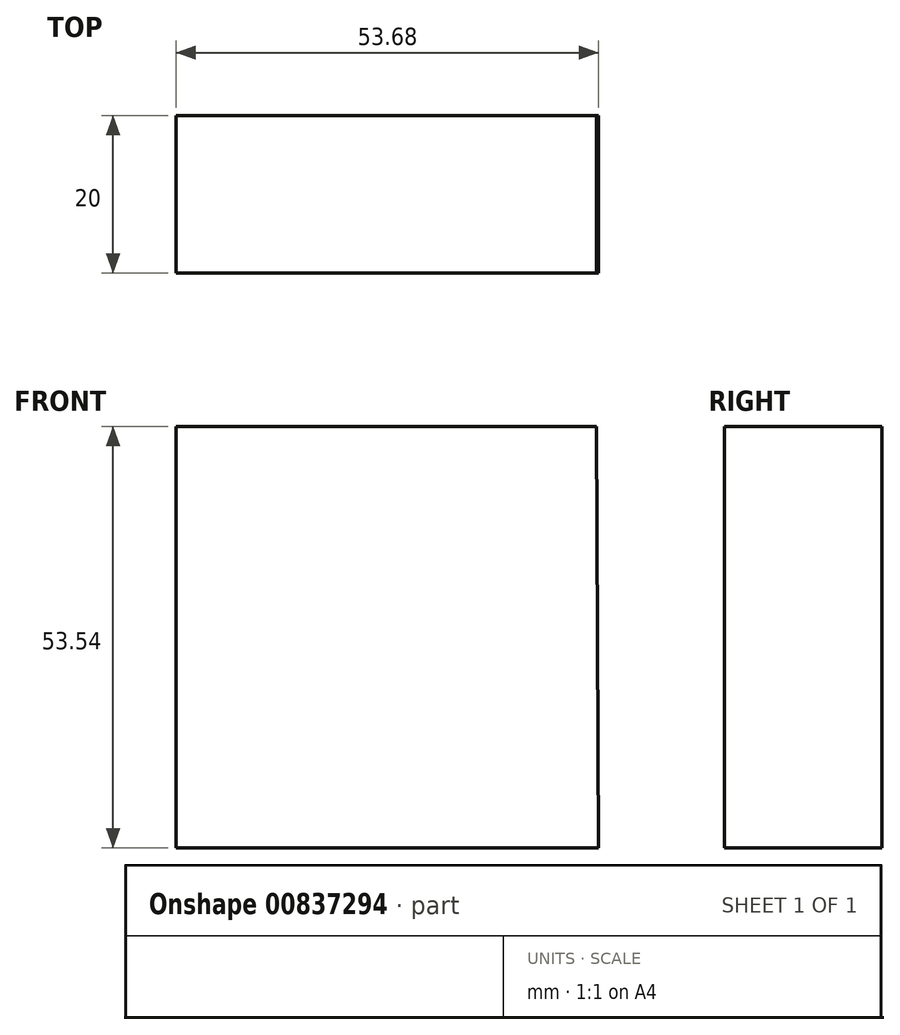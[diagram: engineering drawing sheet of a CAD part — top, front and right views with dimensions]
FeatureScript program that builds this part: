
annotation { "Feature Type Name" : "Feature", "Feature Type Description" : "" }
export const myFeature = defineFeature(function(context is Context, id is Id, definition is map)
    precondition{}
    {
        {
            var Q0;
            Q0=qCreatedBy(makeId("Front.planeOp"),FACE);
            var sketch = newSketch(context, id + "F0", { "sketchPlane" : qUnion([Q0])});
            skLineSegment(sketch, "E0", {"start": v(0, 27.9) * mm, "end": v(0, -25.64) * mm});
            skLineSegment(sketch, "E1", {"start": v(0, 27.9) * mm, "end": v(53.4, 27.9) * mm});
            skLineSegment(sketch, "E2", {"start": v(0, -25.64) * mm, "end": v(53.68, -25.64) * mm});
            skLineSegment(sketch, "E3", {"start": v(53.68, -25.64) * mm, "end": v(53.4, 27.9) * mm});
            skLineSegment(sketch, "E4", {"start": v(6.1, 20.82) * mm, "end": v(6.1, -21.1) * mm});
            skLineSegment(sketch, "E5", {"start": v(6.1, -21.1) * mm, "end": v(46.6, -21.1) * mm});
            skLineSegment(sketch, "E6", {"start": v(6.1, 20.82) * mm, "end": v(46.6, 20.82) * mm});
            skLineSegment(sketch, "E7", {"start": v(46.6, 20.82) * mm, "end": v(46.6, -18.84) * mm});
            skSolve(sketch);
        }
        {
            var Q0;
            Q0=makeQuery(id+"F0.imprint","IMPRINT",FACE,{"disambiguationData":[TD([[makeQuery(id+"F0.imprint","IMPRINT",EDGE,{"derivedFrom":sQuery(id+"F0.wireOp",EDGE,"E0")}),1.0]])]});
            extrude(context, id + "F1", {"entities" : qUnion([Q0]), "depth" : 20 * mm, "offsetDistance" : 25 * mm});
        }
        {
            var Q0;
            Q0 = qSketchRegion(id + "F0", true);
            var Q1;
            Q1=makeQuery(id+"F1.opExtrude","CAP_FACE",FACE,{"disambiguationData":[OSD([sQuery(id+"F0.wireOp",EDGE,"E0"),sQuery(id+"F0.wireOp",EDGE,"E1"),sQuery(id+"F0.wireOp",EDGE,"E2"),sQuery(id+"F0.wireOp",EDGE,"E3")])],"isStart":true});
            extrude(context, id + "F2", {"entities" : qUnion([Q0, Q1]), "operationType" : NewBodyOperationType.ADD, "depth" : 10 * mm, "offsetDistance" : 25 * mm});
        }
    });
